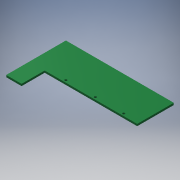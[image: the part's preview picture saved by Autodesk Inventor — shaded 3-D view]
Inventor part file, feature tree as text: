
AUTODESK INVENTOR PART (.ipt)
format: ipt  version: 2018 (Build 220112000, 112)  size: 109,056 bytes
history: native  units: mm
features: extrude x1, sketch x1
ambient origin geometry x8: Origin, YZ Plane, XZ Plane, XY Plane, X Axis, Y Axis, Z Axis, Center Point
bodies: Solid1 (feature_tree)
feature tree (2):
  extrude  "Extrusion1"  Depth=2.5mm
  sketch  "Sketch1"  dims[d8=3.0mm d10=36.8mm d11=75.0mm d15=140.0mm d16=47.5mm d17=20.0mm d18=30.0mm d19=2.5mm d20=0.0mm]
